# Revit family: Softline Zylinderschoss
name_source: partatom
category: HLS-Bauteile
revit_build: Autodesk Revit 2018 (Build: 20170223_1515(x64)
units: mm (PartAtom-declared; Revit-internal decimal feet)

## family parameters
Basisbauteil = Wand
Beim Laden mit Abzugskörper schneiden = Nein
Bemaßung runder Anschluss = Durchmesser verwenden
Gemeinsam genutzt = Nein
Immer vertikal = Ja
Raumberechnungspunkt = Nein
Teiletyp = Normal

## types (20) — shared parameters
Binner = 18.5 mm
H0 = 1650 mm
T1 = 2 mm  [stored 0.00656168 ft]
T2 = 24 mm
TGap = 2.5 mm  [stored 0.0082021 ft]
T_plate = 1 mm  [stored 0.00328084 ft]
Tz = 26 mm
Vb = 32.5 mm
Vh = 32.5 mm

## per-type parameters (varying)
| type | B | B1 | B2_Max | B2_min | B3 | B4 | B5 | Bz | Dlock | H | H1 | H2_Max | H2_Min | H3 | H4 | H5 | HAN | Hz |
| Weiß RAL9016 - 600x600 | 600 mm | 598 mm | 612 mm | 600 mm | 635 mm | 595 mm | 594 mm | 700 mm | 198 mm  [stored 0.649606 ft] | 600 mm | 598 mm | 612 mm | 600 mm | 635 mm | 595 mm | 594 mm | 20571 | 700 mm |
| Weiß RAL9016 - 200X200 | 200 mm  [stored 0.656168 ft] | 198 mm  [stored 0.649606 ft] | 212 mm | 200 mm  [stored 0.656168 ft] | 235 mm | 195 mm | 194 mm | 300 mm | 64.7 mm | 200 mm  [stored 0.656168 ft] | 198 mm  [stored 0.649606 ft] | 212 mm | 200 mm  [stored 0.656168 ft] | 235 mm | 195 mm | 194 mm | 20562 | 300 mm |
| Weiß RAL9016 - 300X300 | 300 mm | 298 mm | 312 mm | 300 mm | 335 mm | 295 mm | 294 mm | 400 mm | 98 mm  [stored 0.321522 ft] | 300 mm | 298 mm | 312 mm | 300 mm | 335 mm | 295 mm | 294 mm | 20567 | 400 mm |
| Weiß RAL9016 - 400X400 | 400 mm | 398 mm | 412 mm | 400 mm | 435 mm | 395 mm | 394 mm | 500 mm | 131.3 mm | 400 mm | 398 mm | 412 mm | 400 mm | 435 mm | 395 mm | 394 mm | 20568 | 500 mm |
| Weiß RAL9016 - 500X500 | 500 mm | 498 mm | 512 mm | 500 mm | 535 mm | 495 mm | 494 mm | 600 mm | 164.7 mm | 500 mm | 498 mm | 512 mm | 500 mm | 535 mm | 495 mm | 494 mm | 20570 | 600 mm |
| Weiß RAL9016 - 200X250 | 200 mm  [stored 0.656168 ft] | 198 mm  [stored 0.649606 ft] | 212 mm | 200 mm  [stored 0.656168 ft] | 235 mm | 195 mm | 194 mm | 300 mm | 81.3 mm | 250 mm  [stored 0.82021 ft] | 248 mm  [stored 0.813648 ft] | 262 mm | 250 mm  [stored 0.82021 ft] | 285 mm | 245 mm | 244 mm | 20563 | 350 mm |
| Weiß RAL9016 - 200X300 | 200 mm  [stored 0.656168 ft] | 198 mm  [stored 0.649606 ft] | 212 mm | 200 mm  [stored 0.656168 ft] | 235 mm | 195 mm | 194 mm | 300 mm | 98 mm  [stored 0.321522 ft] | 300 mm | 298 mm | 312 mm | 300 mm | 335 mm | 295 mm | 294 mm | 20564 | 400 mm |
| Weiß RAL9016 - 200X400 | 200 mm  [stored 0.656168 ft] | 198 mm  [stored 0.649606 ft] | 212 mm | 200 mm  [stored 0.656168 ft] | 235 mm | 195 mm | 194 mm | 300 mm | 131.3 mm | 400 mm | 398 mm | 412 mm | 400 mm | 435 mm | 395 mm | 394 mm | 20605 | 500 mm |
| Weiß RAL9016 - 200X500 | 200 mm  [stored 0.656168 ft] | 198 mm  [stored 0.649606 ft] | 212 mm | 200 mm  [stored 0.656168 ft] | 235 mm | 195 mm | 194 mm | 300 mm | 164.7 mm | 500 mm | 498 mm | 512 mm | 500 mm | 535 mm | 495 mm | 494 mm | 20607 | 600 mm |
| Weiß RAL9016 - 200X600 | 200 mm  [stored 0.656168 ft] | 198 mm  [stored 0.649606 ft] | 212 mm | 200 mm  [stored 0.656168 ft] | 235 mm | 195 mm | 194 mm | 300 mm | 198 mm  [stored 0.649606 ft] | 600 mm | 598 mm | 612 mm | 600 mm | 635 mm | 595 mm | 594 mm | 20610 | 700 mm |
| Weiß RAL9016 - 150X200 | 150 mm | 148 mm | 162 mm | 150 mm | 185 mm  [stored 0.606955 ft] | 145 mm  [stored 0.475722 ft] | 144 mm  [stored 0.472441 ft] | 250 mm  [stored 0.82021 ft] | 64.7 mm | 200 mm  [stored 0.656168 ft] | 198 mm  [stored 0.649606 ft] | 212 mm | 200 mm  [stored 0.656168 ft] | 235 mm | 195 mm | 194 mm | 20561 | 300 mm |
| Weiß RAL9016 - 150X150 | 150 mm | 148 mm | 162 mm | 150 mm | 185 mm  [stored 0.606955 ft] | 145 mm  [stored 0.475722 ft] | 144 mm  [stored 0.472441 ft] | 250 mm  [stored 0.82021 ft] | 48 mm | 150 mm | 148 mm | 162 mm | 150 mm | 185 mm  [stored 0.606955 ft] | 145 mm  [stored 0.475722 ft] | 144 mm  [stored 0.472441 ft] | 20560 | 250 mm  [stored 0.82021 ft] |
| Weiß RAL9016 - 250X250 | 250 mm  [stored 0.82021 ft] | 248 mm  [stored 0.813648 ft] | 262 mm | 250 mm  [stored 0.82021 ft] | 285 mm | 245 mm | 244 mm | 350 mm | 81.3 mm | 250 mm  [stored 0.82021 ft] | 248 mm  [stored 0.813648 ft] | 262 mm | 250 mm  [stored 0.82021 ft] | 285 mm | 245 mm | 244 mm | 20565 | 350 mm |
| Weiß RAL9016 - 250X300 | 250 mm  [stored 0.82021 ft] | 248 mm  [stored 0.813648 ft] | 262 mm | 250 mm  [stored 0.82021 ft] | 285 mm | 245 mm | 244 mm | 350 mm | 98 mm  [stored 0.321522 ft] | 300 mm | 298 mm | 312 mm | 300 mm | 335 mm | 295 mm | 294 mm | 20566 | 400 mm |
| Weiß RAL9016 - 300X400 | 300 mm | 298 mm | 312 mm | 300 mm | 335 mm | 295 mm | 294 mm | 400 mm | 131.3 mm | 400 mm | 398 mm | 412 mm | 400 mm | 435 mm | 395 mm | 394 mm | 20606 | 500 mm |
| Weiß RAL9016 - 300X500 | 300 mm | 298 mm | 312 mm | 300 mm | 335 mm | 295 mm | 294 mm | 400 mm | 164.7 mm | 500 mm | 498 mm | 512 mm | 500 mm | 535 mm | 495 mm | 494 mm | 20608 | 600 mm |
| Weiß RAL9016 - 300X600 | 300 mm | 298 mm | 312 mm | 300 mm | 335 mm | 295 mm | 294 mm | 400 mm | 198 mm  [stored 0.649606 ft] | 600 mm | 598 mm | 612 mm | 600 mm | 635 mm | 595 mm | 594 mm | 20611 | 700 mm |
| Weiß RAL9016 - 400X600 | 400 mm | 398 mm | 412 mm | 400 mm | 435 mm | 395 mm | 394 mm | 500 mm | 198 mm  [stored 0.649606 ft] | 600 mm | 598 mm | 612 mm | 600 mm | 635 mm | 595 mm | 594 mm | 20569 | 700 mm |
| Weiß RAL9016 - 400X500 | 400 mm | 398 mm | 412 mm | 400 mm | 435 mm | 395 mm | 394 mm | 500 mm | 164.7 mm | 500 mm | 498 mm | 512 mm | 500 mm | 535 mm | 495 mm | 494 mm | 20609 | 600 mm |
| Weiß RAL9016 - 500X600 | 500 mm | 498 mm | 512 mm | 500 mm | 535 mm | 495 mm | 494 mm | 600 mm | 198 mm  [stored 0.649606 ft] | 600 mm | 598 mm | 612 mm | 600 mm | 635 mm | 595 mm | 594 mm | 20612 | 700 mm |

note: [stored X ft] marks values corroborated as IEEE doubles in the binary element streams (Revit-internal decimal feet)

## geometry (parser evidence)
native form markers: Sweep x2
no freeform markers — native parametric forms only
